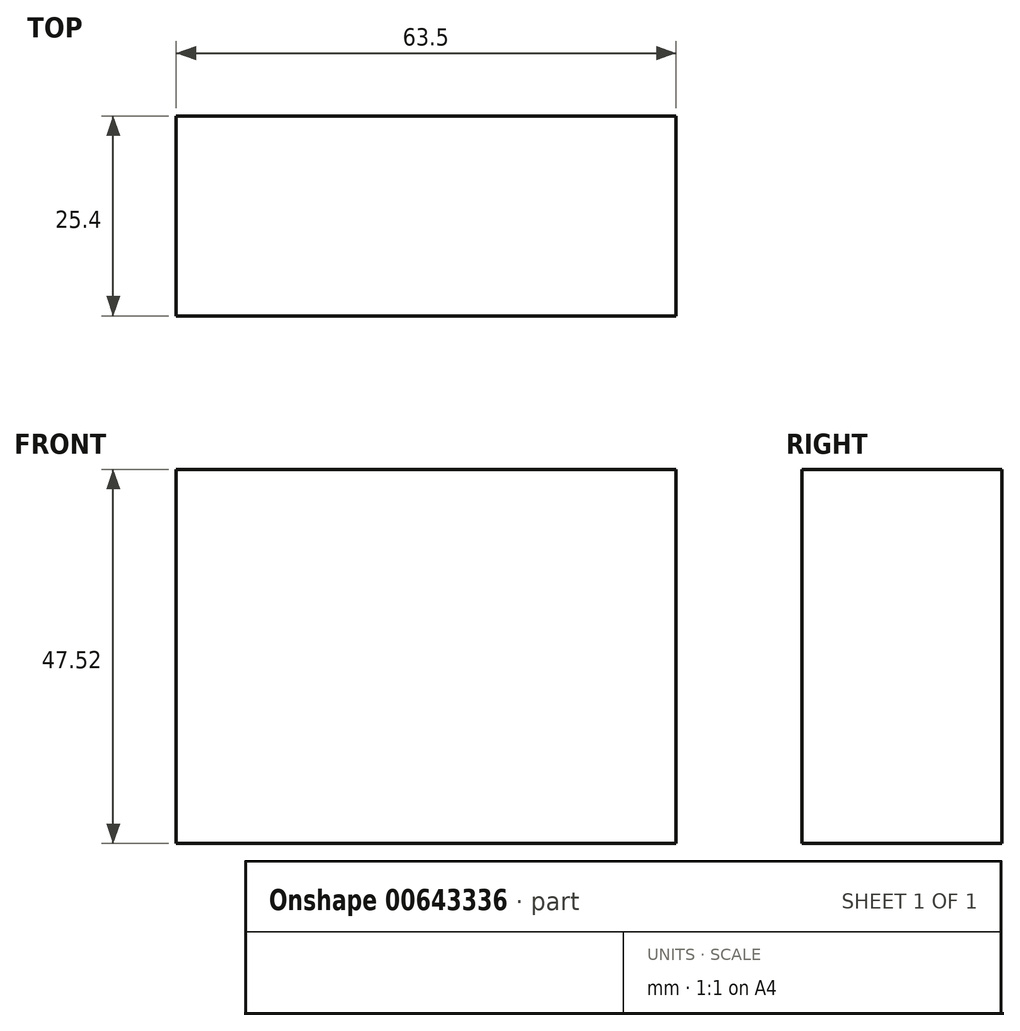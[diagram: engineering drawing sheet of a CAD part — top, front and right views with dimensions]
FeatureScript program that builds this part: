
annotation { "Feature Type Name" : "Feature", "Feature Type Description" : "" }
export const myFeature = defineFeature(function(context is Context, id is Id, definition is map)
    precondition{}
    {
        {
            var Q0;
            Q0=qCreatedBy(makeId("Front.planeOp"),FACE);
            var sketch = newSketch(context, id + "F0", { "sketchPlane" : qUnion([Q0])});
            skLineSegment(sketch, "E0.bottom", {"start": v(-63.5, 47.52) * mm, "end": v(0, 47.52) * mm});
            skLineSegment(sketch, "E0.top", {"start": v(-63.5, 0) * mm, "end": v(0, 0) * mm});
            skLineSegment(sketch, "E0.left", {"start": v(-63.5, 47.52) * mm, "end": v(-63.5, 0) * mm});
            skLineSegment(sketch, "E0.right", {"start": v(0, 47.52) * mm, "end": v(0, 0) * mm});
            skSolve(sketch);
        }
        {
            var Q0;
            Q0=makeQuery(id+"F0.imprint","IMPRINT",FACE,{"disambiguationData":[TD([[makeQuery(id+"F0.imprint","IMPRINT",EDGE,{"derivedFrom":sQuery(id+"F0.wireOp",EDGE,"E0.bottom")}),-1.0]])]});
            extrude(context, id + "F1", {"entities" : qUnion([Q0]), "depth" : 25.4 * mm, "offsetDistance" : 25.4 * mm});
        }
    });
